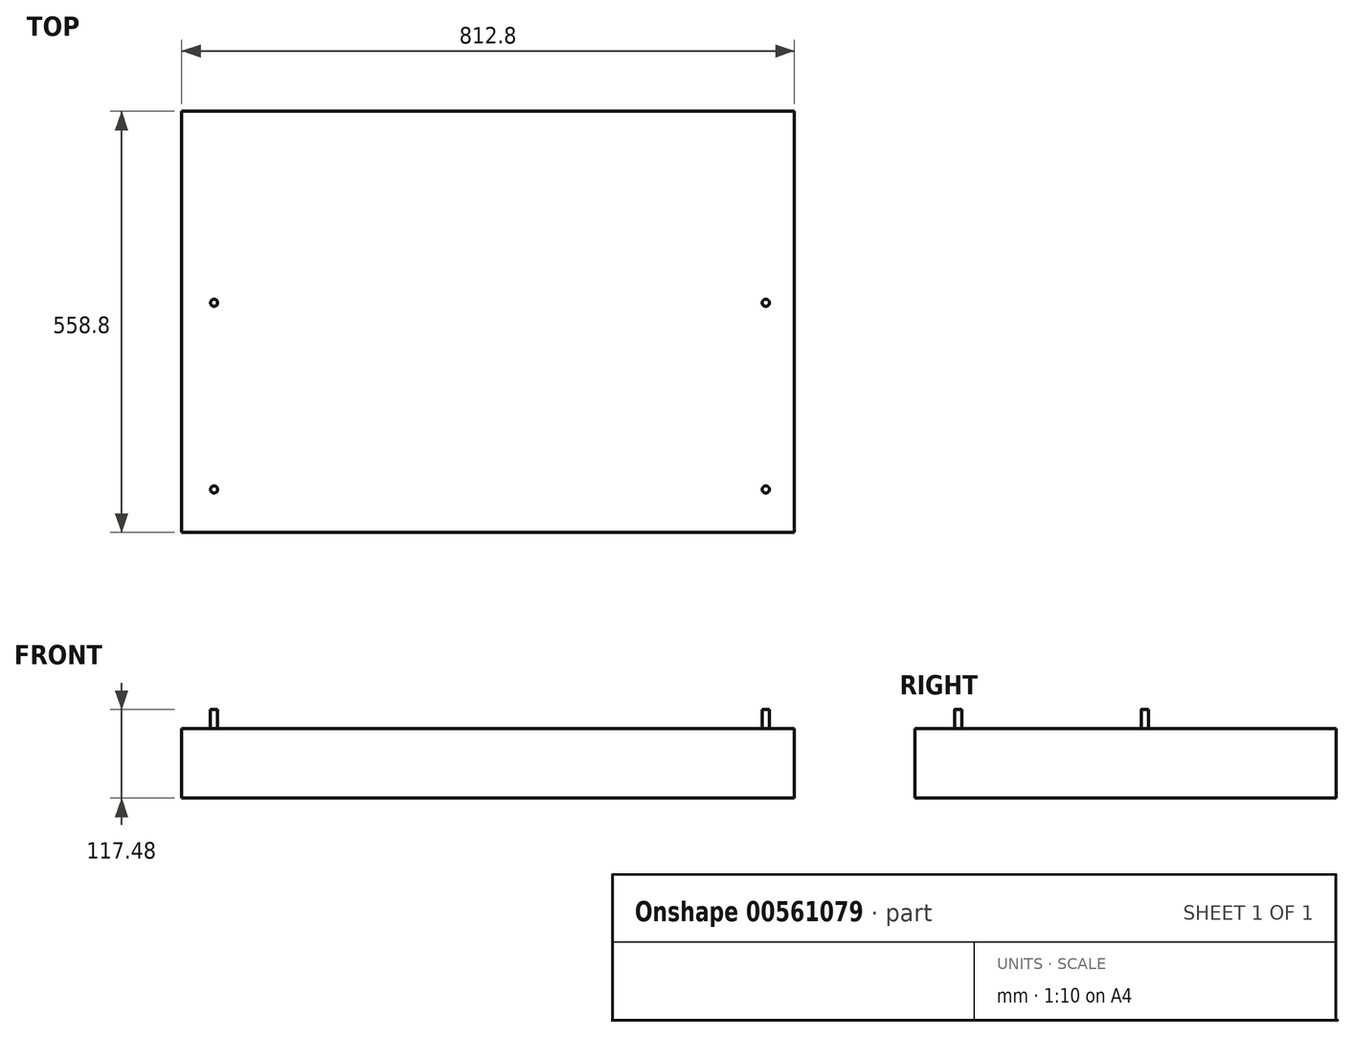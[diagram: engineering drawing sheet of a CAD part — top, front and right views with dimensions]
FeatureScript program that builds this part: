
annotation { "Feature Type Name" : "Feature", "Feature Type Description" : "" }
export const myFeature = defineFeature(function(context is Context, id is Id, definition is map)
    precondition{}
    {
        {
            var Q0;
            Q0=qCreatedBy(makeId("Top.planeOp"),FACE);
            var sketch = newSketch(context, id + "F0", { "sketchPlane" : qUnion([Q0])});
            skLineSegment(sketch, "E0.bottom", {"start": v(-406.4, 279.4) * mm, "end": v(406.4, 279.4) * mm});
            skLineSegment(sketch, "E0.top", {"start": v(-406.4, -279.4) * mm, "end": v(406.4, -279.4) * mm});
            skLineSegment(sketch, "E0.left", {"start": v(-406.4, 279.4) * mm, "end": v(-406.4, -279.4) * mm});
            skLineSegment(sketch, "E0.right", {"start": v(406.4, 279.4) * mm, "end": v(406.4, -279.4) * mm});
            skPoint(sketch, "E0.middle", {"position": v(0, 0) * mm});
            skSolve(sketch);
        }
        {
            var Q0;
            Q0 = qSketchRegion(id + "F0", true);
            extrude(context, id + "F1", {"entities" : qUnion([Q0]), "depth" : 92.07 * mm, "offsetDistance" : 25.4 * mm});
        }
        {
            var Q0;
            Q0=makeQuery(id+"F1.opExtrude","CAP_FACE",FACE,{"disambiguationData":[OSD([sQuery(id+"F0.wireOp",EDGE,"E0.bottom"),sQuery(id+"F0.wireOp",EDGE,"E0.top"),sQuery(id+"F0.wireOp",EDGE,"E0.left"),sQuery(id+"F0.wireOp",EDGE,"E0.right")])],"isStart":false});
            var sketch = newSketch(context, id + "F2", { "sketchPlane" : qUnion([Q0])});
            skPoint(sketch, "E1", {"position": v(368.3, 25.4) * mm});
            skPoint(sketch, "E2", {"position": v(368.3, -222.25) * mm});
            skPoint(sketch, "E3", {"position": v(-363.54, -222.25) * mm});
            skPoint(sketch, "E4", {"position": v(-363.54, 25.4) * mm});
            skCircle(sketch, "E5", {"center": v(-363.54, 25.4) * mm, "radius": 4.76 * mm});
            skCircle(sketch, "E6", {"center": v(-363.54, -222.25) * mm, "radius": 4.76 * mm});
            skCircle(sketch, "E7", {"center": v(368.3, 25.4) * mm, "radius": 4.76 * mm});
            skCircle(sketch, "E8", {"center": v(368.3, -222.25) * mm, "radius": 4.76 * mm});
            skSolve(sketch);
        }
        {
            var Q0;
            Q0 = qSketchRegion(id + "F2", true);
            extrude(context, id + "F3", {"entities" : qUnion([Q0]), "operationType" : NewBodyOperationType.ADD, "depth" : 25.4 * mm, "offsetDistance" : 25.4 * mm});
        }
    });
